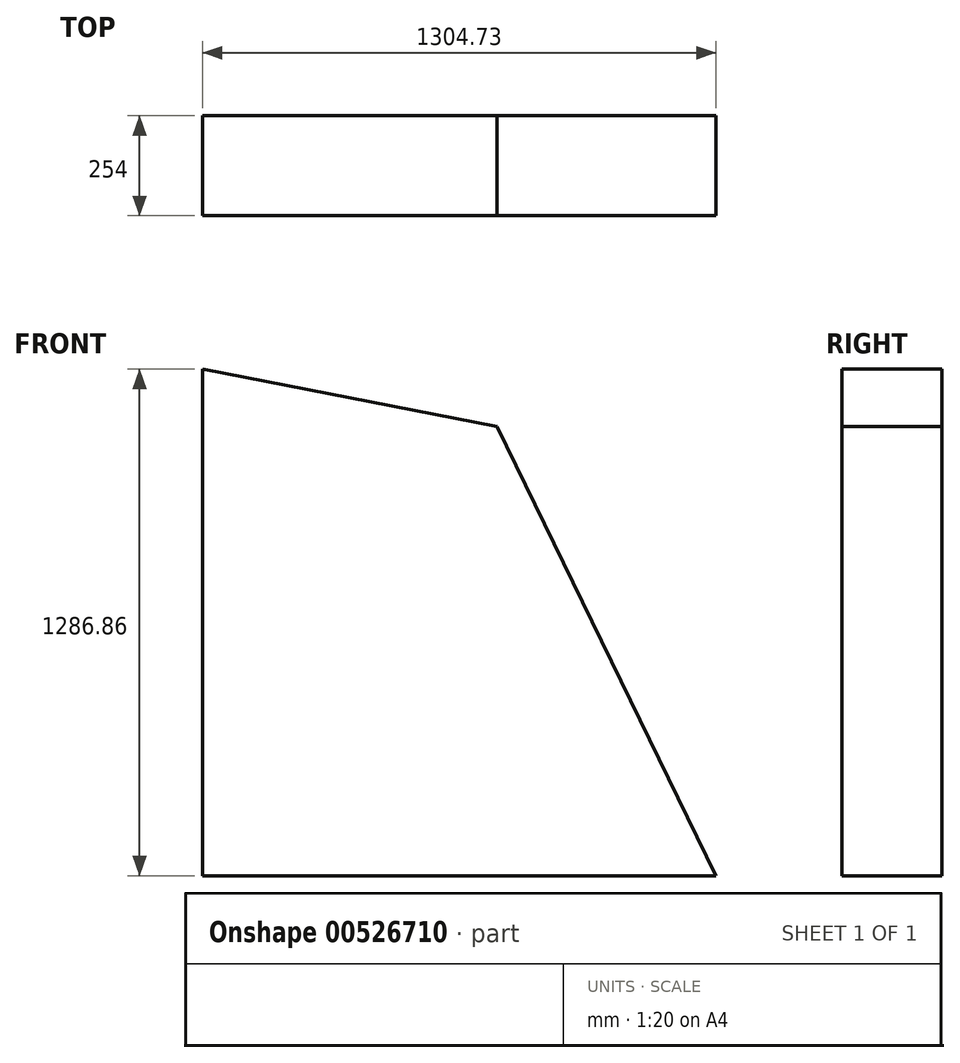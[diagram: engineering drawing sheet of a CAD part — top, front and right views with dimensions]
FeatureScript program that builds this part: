
annotation { "Feature Type Name" : "Feature", "Feature Type Description" : "" }
export const myFeature = defineFeature(function(context is Context, id is Id, definition is map)
    precondition{}
    {
        {
            var Q0;
            Q0=qCreatedBy(makeId("Front.planeOp"),FACE);
            var sketch = newSketch(context, id + "F0", { "sketchPlane" : qUnion([Q0])});
            skLineSegment(sketch, "E0", {"start": v(0, 0) * mm, "end": v(-556.73, 1141.47) * mm});
            skLineSegment(sketch, "E1", {"start": v(-556.73, 1141.47) * mm, "end": v(-1304.73, 1286.86) * mm});
            skLineSegment(sketch, "E2", {"start": v(-1304.73, 1286.86) * mm, "end": v(-1304.73, 0) * mm});
            skLineSegment(sketch, "E3", {"start": v(-1304.73, 0) * mm, "end": v(0, 0) * mm});
            skSolve(sketch);
        }
        {
            var Q0;
            Q0 = qSketchRegion(id + "F0", true);
            extrude(context, id + "F1", {"entities" : qUnion([Q0]), "depth" : 254 * mm, "offsetDistance" : 25.4 * mm});
        }
    });
